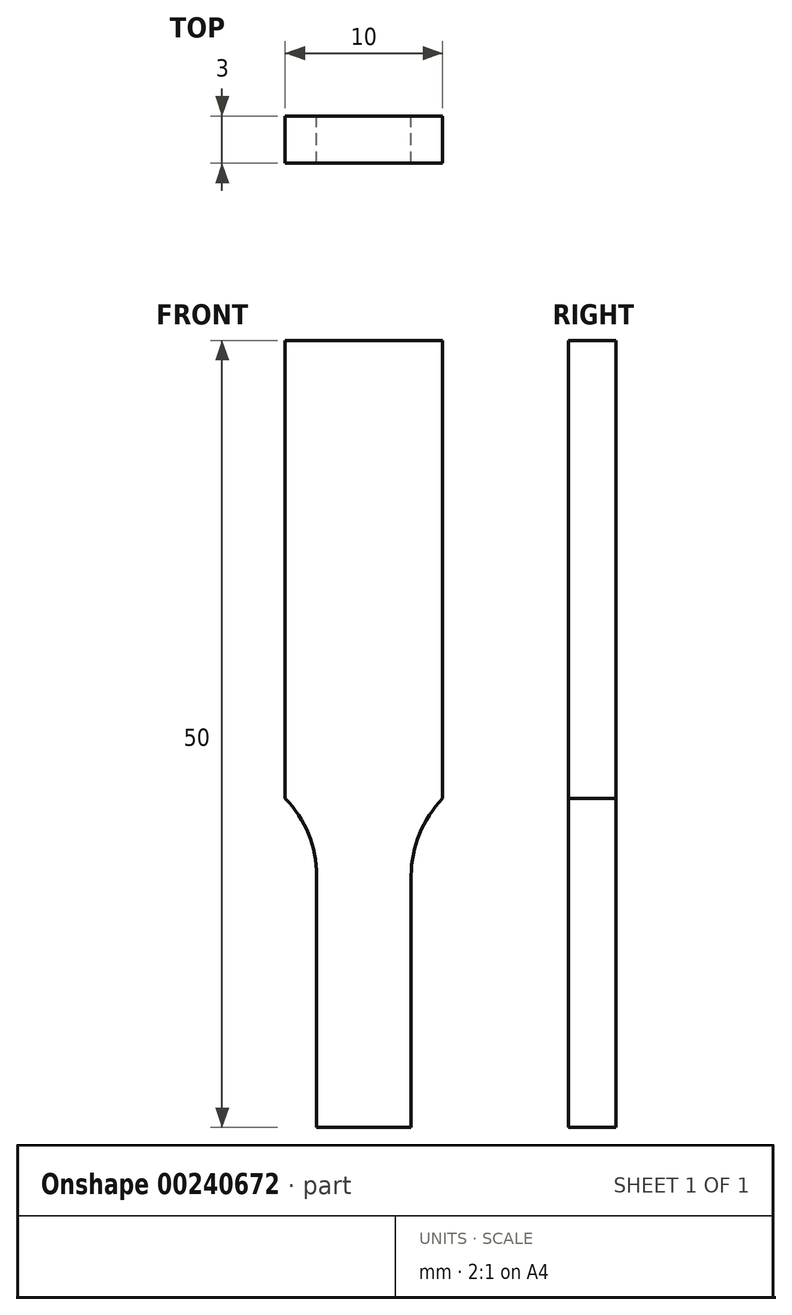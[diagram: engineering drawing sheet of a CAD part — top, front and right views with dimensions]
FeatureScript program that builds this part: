
annotation { "Feature Type Name" : "Feature", "Feature Type Description" : "" }
export const myFeature = defineFeature(function(context is Context, id is Id, definition is map)
    precondition{}
    {
        {
            var Q0;
            Q0=qCreatedBy(makeId("Front.planeOp"),FACE);
            var sketch = newSketch(context, id + "F0", { "sketchPlane" : qUnion([Q0])});
            skLineSegment(sketch, "E0.right", {"start": v(3, 0) * mm, "end": v(3, 16) * mm});
            skLineSegment(sketch, "E1.top", {"start": v(0, 50) * mm, "end": v(5, 50) * mm});
            skLineSegment(sketch, "E1.right", {"start": v(5, 20.9) * mm, "end": v(5, 50) * mm});
            skArc(sketch, "E2", {"start": v(3, 16) * mm, "mid": v(3.52, 18.65) * mm, "end": v(5, 20.9) * mm});
            skArc(sketch, "E3.MirrorCS", {"start": v(-3, 16) * mm, "mid": v(-3.52, 18.65) * mm, "end": v(-5, 20.9) * mm});
            skLineSegment(sketch, "E4.MirrorCS", {"start": v(0, 50) * mm, "end": v(-5, 50) * mm});
            skLineSegment(sketch, "E5.MirrorCS", {"start": v(-5, 20.9) * mm, "end": v(-5, 50) * mm});
            skLineSegment(sketch, "E6.MirrorCS", {"start": v(-3, 0) * mm, "end": v(-3, 16) * mm});
            skPoint(sketch, "E7.MirrorCS.start.orphan", {"position": v(3, 0) * mm});
            skPoint(sketch, "E8.MirrorCS.start.orphan", {"position": v(-3, 0) * mm});
            skLineSegment(sketch, "E9", {"start": v(-3, 0) * mm, "end": v(3, 0) * mm});
            skSolve(sketch);
        }
        {
            var Q0;
            Q0=qSketchRegion(id+"F0",true);
            extrude(context, id + "F1", {"entities" : qUnion([Q0]), "depth" : 3 * mm});
        }
    });
